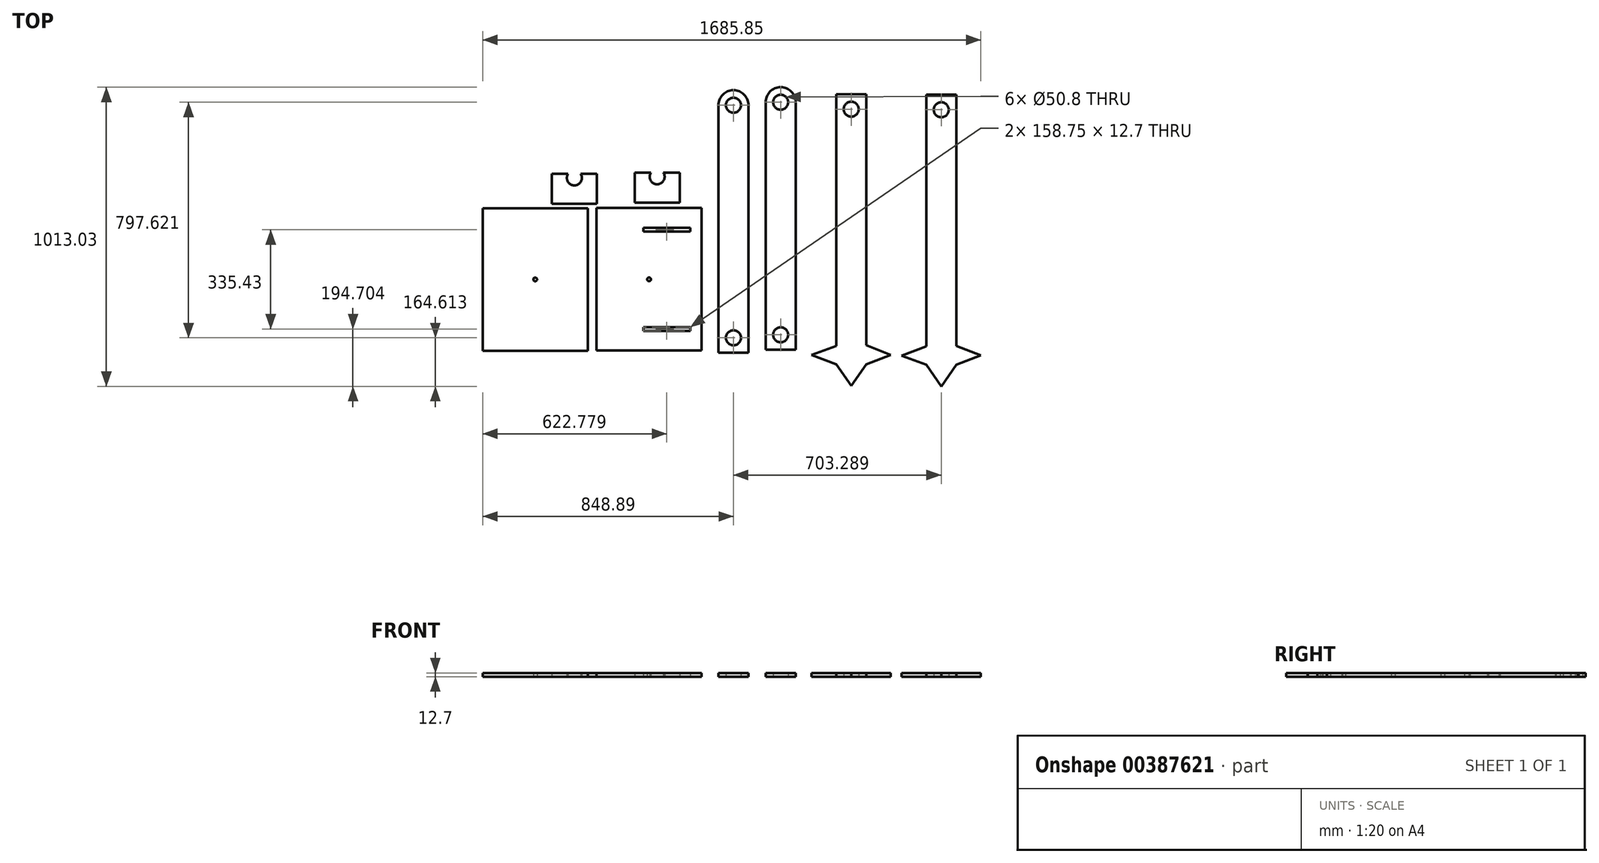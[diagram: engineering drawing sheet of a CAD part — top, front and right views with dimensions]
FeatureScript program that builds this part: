
annotation { "Feature Type Name" : "Feature", "Feature Type Description" : "" }
export const myFeature = defineFeature(function(context is Context, id is Id, definition is map)
    precondition{}
    {
        {
            var Q0;
            Q0=qCreatedBy(makeId("Top.planeOp"),FACE);
            var sketch = newSketch(context, id + "F0", { "sketchPlane" : qUnion([Q0])});
            skLineSegment(sketch, "E0.right", {"start": v(-216.91, 84.83) * mm, "end": v(-216.91, -397.77) * mm});
            skCircle(sketch, "E1", {"center": v(-394.71, -156.47) * mm, "radius": 6.35 * mm});
            skLineSegment(sketch, "E2.top", {"start": v(-723.91, 99.39) * mm, "end": v(-571.51, 99.39) * mm});
            skLineSegment(sketch, "E2.left", {"start": v(-723.91, 200.99) * mm, "end": v(-723.91, 99.39) * mm});
            skLineSegment(sketch, "E2.right", {"start": v(-571.51, 200.99) * mm, "end": v(-571.51, 99.39) * mm});
            skLineSegment(sketch, "E3", {"start": v(-647.71, 200.99) * mm, "end": v(-647.71, 186.9) * mm, "construction": true});
            skArc(sketch, "E4", {"start": v(-668.84, 200.99) * mm, "mid": v(-647.71, 161.53) * mm, "end": v(-626.58, 200.99) * mm});
            skLineSegment(sketch, "E5", {"start": v(-723.91, 200.99) * mm, "end": v(-668.84, 200.99) * mm});
            skLineSegment(sketch, "E6", {"start": v(-626.58, 200.99) * mm, "end": v(-571.51, 200.99) * mm});
            skLineSegment(sketch, "E7.top", {"start": v(-443.74, 103.28) * mm, "end": v(-291.34, 103.28) * mm});
            skLineSegment(sketch, "E7.left", {"start": v(-443.74, 204.88) * mm, "end": v(-443.74, 103.28) * mm});
            skLineSegment(sketch, "E7.right", {"start": v(-291.34, 204.88) * mm, "end": v(-291.34, 103.28) * mm});
            skLineSegment(sketch, "E8", {"start": v(-367.54, 204.88) * mm, "end": v(-367.54, 190.78) * mm, "construction": true});
            skArc(sketch, "E9", {"start": v(-388.67, 204.88) * mm, "mid": v(-367.54, 165.43) * mm, "end": v(-346.4, 204.88) * mm});
            skLineSegment(sketch, "E10", {"start": v(-443.74, 204.88) * mm, "end": v(-388.67, 204.88) * mm});
            skLineSegment(sketch, "E11", {"start": v(-346.4, 204.88) * mm, "end": v(-291.34, 204.88) * mm});
            skLineSegment(sketch, "E12", {"start": v(-668.84, 200.99) * mm, "end": v(-626.58, 200.99) * mm, "construction": true});
            skLineSegment(sketch, "E13.bottom", {"start": v(-411.53, 17.6) * mm, "end": v(-259.13, 17.6) * mm});
            skLineSegment(sketch, "E13.top", {"start": v(-411.53, 4.9) * mm, "end": v(-259.13, 4.9) * mm});
            skLineSegment(sketch, "E14", {"start": v(-335.33, 17.6) * mm, "end": v(-335.33, 4.9) * mm, "construction": true});
            skLineSegment(sketch, "E15", {"start": v(-411.53, 11.24) * mm, "end": v(-259.13, 11.24) * mm, "construction": true});
            skLineSegment(sketch, "E16", {"start": v(-411.53, 11.24) * mm, "end": v(-462.33, 11.24) * mm, "construction": true});
            skLineSegment(sketch, "E17.MirrorCS", {"start": v(-411.53, -317.84) * mm, "end": v(-259.13, -317.84) * mm});
            skLineSegment(sketch, "E18.MirrorCS", {"start": v(-411.53, -330.54) * mm, "end": v(-259.13, -330.54) * mm});
            skLineSegment(sketch, "E19.MirrorCS", {"start": v(-411.53, -324.19) * mm, "end": v(-259.13, -324.19) * mm, "construction": true});
            skLineSegment(sketch, "E20.MirrorCS", {"start": v(-411.53, -324.19) * mm, "end": v(-462.33, -324.19) * mm, "construction": true});
            skLineSegment(sketch, "E21", {"start": v(-335.33, -330.54) * mm, "end": v(-335.33, -406.15) * mm});
            skLineSegment(sketch, "E22", {"start": v(-335.33, 17.6) * mm, "end": v(-335.33, 76.45) * mm});
            skLineSegment(sketch, "E23", {"start": v(-216.91, 84.83) * mm, "end": v(-572.51, 84.83) * mm});
            skLineSegment(sketch, "E24", {"start": v(-216.91, -397.77) * mm, "end": v(-572.51, -397.77) * mm});
            skLineSegment(sketch, "E25", {"start": v(-572.51, 84.83) * mm, "end": v(-572.51, -397.77) * mm});
            skLineSegment(sketch, "E26.right", {"start": v(-602.5, 84.74) * mm, "end": v(-602.5, -397.86) * mm});
            skCircle(sketch, "E27", {"center": v(-780.3, -156.56) * mm, "radius": 6.35 * mm});
            skLineSegment(sketch, "E28.left", {"start": v(-797.13, 17.5) * mm, "end": v(-797.13, 4.8) * mm});
            skLineSegment(sketch, "E28.right", {"start": v(-644.73, 17.5) * mm, "end": v(-644.73, 4.8) * mm});
            skLineSegment(sketch, "E29", {"start": v(-720.93, 17.5) * mm, "end": v(-720.93, 4.8) * mm, "construction": true});
            skLineSegment(sketch, "E30.MirrorCS", {"start": v(-797.13, -330.63) * mm, "end": v(-797.13, -317.93) * mm});
            skLineSegment(sketch, "E31.MirrorCS", {"start": v(-644.73, -330.63) * mm, "end": v(-644.73, -317.93) * mm});
            skLineSegment(sketch, "E32", {"start": v(-720.93, 17.5) * mm, "end": v(-720.93, 96.92) * mm});
            skLineSegment(sketch, "E33", {"start": v(-602.5, 84.74) * mm, "end": v(-958.1, 84.74) * mm});
            skLineSegment(sketch, "E34", {"start": v(-602.5, -397.86) * mm, "end": v(-958.1, -397.86) * mm});
            skLineSegment(sketch, "E35", {"start": v(-958.1, 84.74) * mm, "end": v(-958.1, -397.86) * mm});
            skLineSegment(sketch, "E36", {"start": v(-780.3, -156.56) * mm, "end": v(-602.5, -156.56) * mm, "construction": true});
            skLineSegment(sketch, "E37", {"start": v(-780.3, -156.56) * mm, "end": v(-958.1, -156.56) * mm, "construction": true});
            skLineSegment(sketch, "E38", {"start": v(-394.71, -156.47) * mm, "end": v(-216.91, -156.47) * mm, "construction": true});
            skLineSegment(sketch, "E39", {"start": v(-394.71, -156.47) * mm, "end": v(-572.51, -156.47) * mm, "construction": true});
            skLineSegment(sketch, "E40", {"start": v(-572.51, -82.6) * mm, "end": v(-216.91, -82.6) * mm, "construction": true});
            skLineSegment(sketch, "E41", {"start": v(-0.34, -394.86) * mm, "end": v(101.26, -394.86) * mm});
            skLineSegment(sketch, "E42", {"start": v(50.46, -394.86) * mm, "end": v(50.46, -344.06) * mm, "construction": true});
            skCircle(sketch, "E43", {"center": v(50.46, -344.06) * mm, "radius": 25.4 * mm});
            skLineSegment(sketch, "E44", {"start": v(-0.34, -394.86) * mm, "end": v(-0.34, 443.34) * mm});
            skLineSegment(sketch, "E45", {"start": v(101.26, -394.86) * mm, "end": v(101.26, 443.34) * mm});
            skArc(sketch, "E46", {"start": v(101.26, 443.34) * mm, "mid": v(50.46, 494.14) * mm, "end": v(-0.34, 443.34) * mm});
            skCircle(sketch, "E47", {"center": v(50.46, 443.34) * mm, "radius": 25.4 * mm});
            skLineSegment(sketch, "E48.bottom", {"start": v(238.37, 470.37) * mm, "end": v(339.97, 470.37) * mm});
            skLineSegment(sketch, "E48.top", {"start": v(238.37, -444.03) * mm, "end": v(339.97, -444.03) * mm});
            skLineSegment(sketch, "E48.left", {"start": v(238.37, 470.37) * mm, "end": v(238.37, -444.03) * mm});
            skLineSegment(sketch, "E48.right", {"start": v(339.97, 470.37) * mm, "end": v(339.97, -444.03) * mm});
            skPoint(sketch, "E49.centerSnap0", {"position": v(289.17, 470.37) * mm});
            skPoint(sketch, "E50.endSnap0", {"position": v(289.17, -444.03) * mm});
            skLineSegment(sketch, "E51", {"start": v(238.37, -444.03) * mm, "end": v(289.17, -516.98) * mm});
            skLineSegment(sketch, "E52", {"start": v(289.17, -516.98) * mm, "end": v(339.97, -444.03) * mm});
            skLineSegment(sketch, "E53", {"start": v(339.97, -444.03) * mm, "end": v(422.84, -411.85) * mm});
            skLineSegment(sketch, "E54", {"start": v(422.84, -411.85) * mm, "end": v(339.97, -379.67) * mm});
            skLineSegment(sketch, "E55", {"start": v(238.37, -444.03) * mm, "end": v(155.09, -412.93) * mm});
            skLineSegment(sketch, "E56", {"start": v(155.09, -412.93) * mm, "end": v(238.37, -381.83) * mm});
            skLineSegment(sketch, "E57", {"start": v(50.46, 417.94) * mm, "end": v(50.46, -318.66) * mm, "construction": true});
            skLineSegment(sketch, "E58", {"start": v(-160.02, -405.08) * mm, "end": v(-58.42, -405.08) * mm});
            skCircle(sketch, "E59", {"center": v(-109.22, -354.28) * mm, "radius": 25.4 * mm});
            skLineSegment(sketch, "E60", {"start": v(-160.02, -405.08) * mm, "end": v(-160.02, 433.12) * mm});
            skLineSegment(sketch, "E61", {"start": v(-58.42, -405.08) * mm, "end": v(-58.42, 433.12) * mm});
            skArc(sketch, "E62", {"start": v(-58.42, 433.12) * mm, "mid": v(-109.22, 483.92) * mm, "end": v(-160.02, 433.12) * mm});
            skCircle(sketch, "E63", {"center": v(-109.22, 433.12) * mm, "radius": 25.4 * mm});
            skLineSegment(sketch, "E64", {"start": v(-109.22, 407.72) * mm, "end": v(-109.22, -328.88) * mm, "construction": true});
            skLineSegment(sketch, "E65", {"start": v(289.17, 470.37) * mm, "end": v(289.17, 444.97) * mm, "construction": true});
            skLineSegment(sketch, "E66", {"start": v(289.17, 444.97) * mm, "end": v(289.17, 419.57) * mm, "construction": true});
            skCircle(sketch, "E67", {"center": v(289.17, 419.57) * mm, "radius": 25.4 * mm});
            skLineSegment(sketch, "E68.bottom", {"start": v(543.27, 468.47) * mm, "end": v(644.87, 468.47) * mm});
            skLineSegment(sketch, "E68.top", {"start": v(543.27, -445.93) * mm, "end": v(644.87, -445.93) * mm});
            skLineSegment(sketch, "E68.left", {"start": v(543.27, 468.47) * mm, "end": v(543.27, -445.93) * mm});
            skLineSegment(sketch, "E68.right", {"start": v(644.87, 468.47) * mm, "end": v(644.87, -445.93) * mm});
            skPoint(sketch, "E69.centerSnap0", {"position": v(594.07, 468.47) * mm});
            skPoint(sketch, "E70.endSnap0", {"position": v(594.07, -445.93) * mm});
            skLineSegment(sketch, "E71", {"start": v(543.27, -445.93) * mm, "end": v(594.07, -518.89) * mm});
            skLineSegment(sketch, "E72", {"start": v(594.07, -518.89) * mm, "end": v(644.87, -445.93) * mm});
            skLineSegment(sketch, "E73", {"start": v(644.87, -445.93) * mm, "end": v(727.74, -413.75) * mm});
            skLineSegment(sketch, "E74", {"start": v(727.74, -413.75) * mm, "end": v(644.87, -381.58) * mm});
            skLineSegment(sketch, "E75", {"start": v(543.27, -445.93) * mm, "end": v(459.99, -414.83) * mm});
            skLineSegment(sketch, "E76", {"start": v(459.99, -414.83) * mm, "end": v(543.27, -383.74) * mm});
            skLineSegment(sketch, "E77", {"start": v(594.07, 468.47) * mm, "end": v(594.07, 443.07) * mm, "construction": true});
            skLineSegment(sketch, "E78", {"start": v(594.07, 443.07) * mm, "end": v(594.07, 417.67) * mm, "construction": true});
            skCircle(sketch, "E79", {"center": v(594.07, 417.67) * mm, "radius": 25.4 * mm});
            skLineSegment(sketch, "E80", {"start": v(-109.22, -328.88) * mm, "end": v(-109.22, -379.68) * mm, "construction": true});
            skLineSegment(sketch, "E81", {"start": v(-259.13, -317.84) * mm, "end": v(-255.96, -317.84) * mm});
            skLineSegment(sketch, "E82", {"start": v(-255.96, -317.84) * mm, "end": v(-255.96, -330.54) * mm});
            skLineSegment(sketch, "E83", {"start": v(-259.13, -330.54) * mm, "end": v(-255.96, -330.54) * mm});
            skLineSegment(sketch, "E84", {"start": v(-335.33, -330.54) * mm, "end": v(-335.33, -317.84) * mm, "construction": true});
            skLineSegment(sketch, "E85.MirrorCS", {"start": v(-259.13, -330.54) * mm, "end": v(-411.53, -330.54) * mm});
            skLineSegment(sketch, "E86.MirrorCS", {"start": v(-411.53, -317.84) * mm, "end": v(-414.7, -317.84) * mm});
            skLineSegment(sketch, "E87.MirrorCS", {"start": v(-259.13, -324.19) * mm, "end": v(-411.53, -324.19) * mm, "construction": true});
            skLineSegment(sketch, "E88.MirrorCS", {"start": v(-414.7, -317.84) * mm, "end": v(-414.7, -330.54) * mm});
            skLineSegment(sketch, "E89.MirrorCS", {"start": v(-411.53, -330.54) * mm, "end": v(-414.7, -330.54) * mm});
            skLineSegment(sketch, "E90.MirrorCS", {"start": v(-259.13, -317.84) * mm, "end": v(-411.53, -317.84) * mm});
            skLineSegment(sketch, "E91", {"start": v(-411.53, -330.54) * mm, "end": v(-411.53, -317.84) * mm, "construction": true});
            skLineSegment(sketch, "E92", {"start": v(-259.13, -330.54) * mm, "end": v(-259.13, -317.84) * mm, "construction": true});
            skLineSegment(sketch, "E93.MirrorCS", {"start": v(-411.53, 17.6) * mm, "end": v(-414.7, 17.6) * mm});
            skLineSegment(sketch, "E94.MirrorCS", {"start": v(-411.53, 4.9) * mm, "end": v(-414.7, 4.9) * mm});
            skLineSegment(sketch, "E95.MirrorCS", {"start": v(-414.7, 4.9) * mm, "end": v(-414.7, 17.6) * mm});
            skLineSegment(sketch, "E96.MirrorCS", {"start": v(-259.13, 17.6) * mm, "end": v(-255.96, 17.6) * mm});
            skLineSegment(sketch, "E97.MirrorCS", {"start": v(-259.13, 4.9) * mm, "end": v(-255.96, 4.9) * mm});
            skLineSegment(sketch, "E98.MirrorCS", {"start": v(-255.96, 4.9) * mm, "end": v(-255.96, 17.6) * mm});
            skLineSegment(sketch, "E99", {"start": v(-411.53, 4.9) * mm, "end": v(-411.53, 17.6) * mm, "construction": true});
            skLineSegment(sketch, "E100", {"start": v(-259.13, 4.9) * mm, "end": v(-259.13, 17.6) * mm, "construction": true});
            skSolve(sketch);
        }
        {
            var Q0;
            Q0 = qSketchRegion(id + "F0", true);
            extrude(context, id + "F1", {"entities" : qUnion([Q0]), "depth" : 12.7 * mm});
        }
    });
